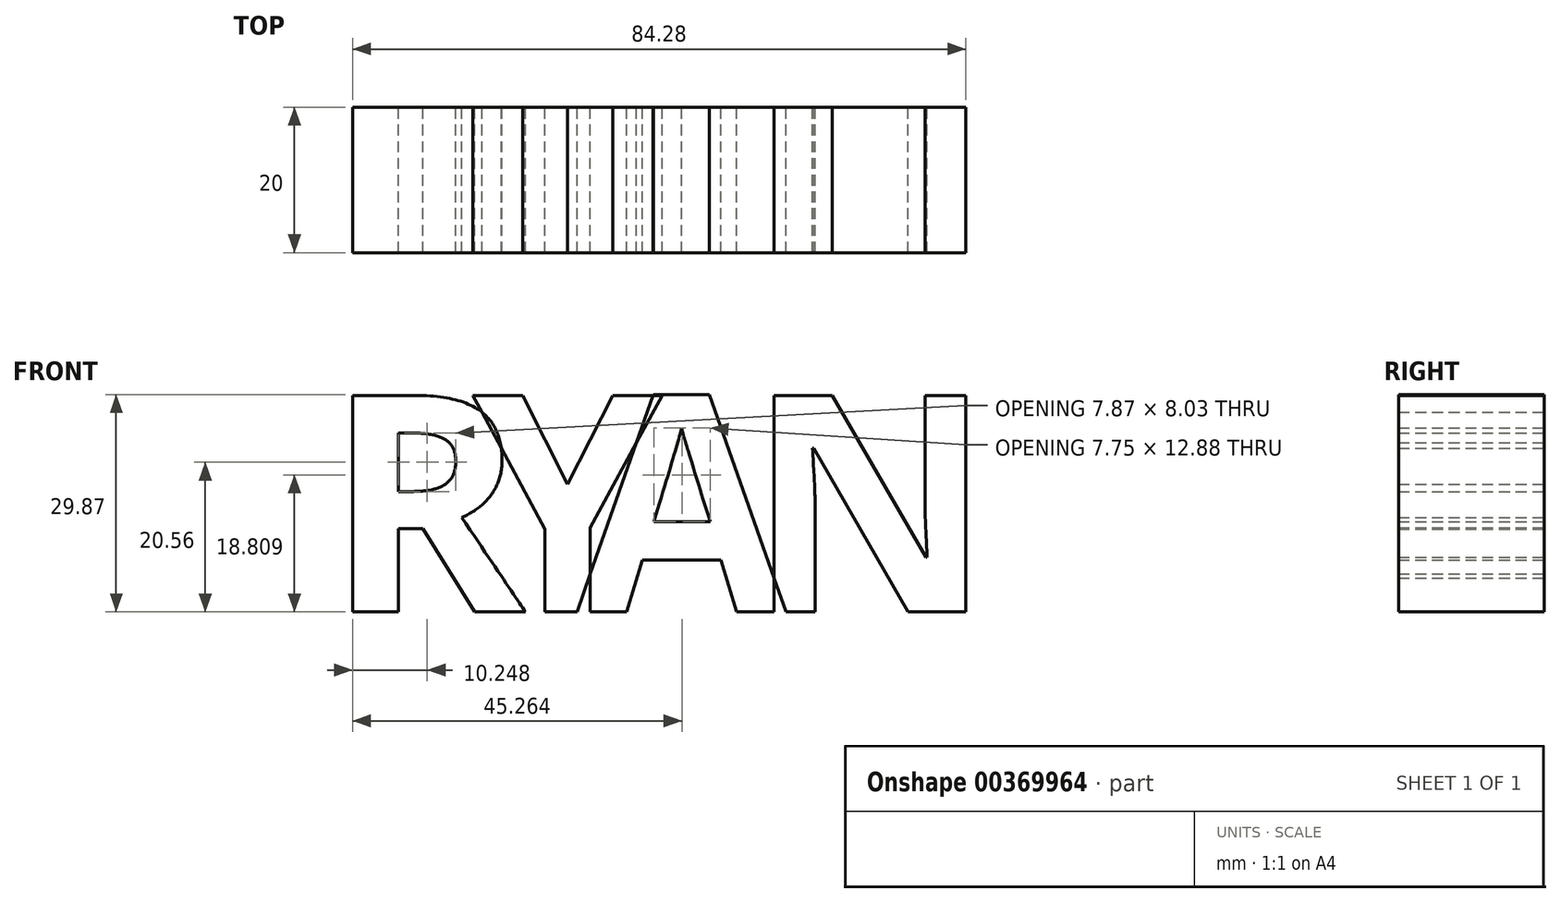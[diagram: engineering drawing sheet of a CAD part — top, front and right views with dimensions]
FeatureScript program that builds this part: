
annotation { "Feature Type Name" : "Feature", "Feature Type Description" : "" }
export const myFeature = defineFeature(function(context is Context, id is Id, definition is map)
    precondition{}
    {
        {
            var Q0;
            Q0=qCreatedBy(makeId("Front.planeOp"),FACE);
            var sketch = newSketch(context, id + "F0", { "sketchPlane" : qUnion([Q0])});
            skText(sketch, "E0", { "text": "R", "fontName": "OpenSans-Bold.ttf"});
            skText(sketch, "E1", { "text": "Y", "fontName": "OpenSans-Bold.ttf"});
            skText(sketch, "E2", { "text": "A", "fontName": "OpenSans-Bold.ttf"});
            skText(sketch, "E3", { "text": "N", "fontName": "OpenSans-Bold.ttf"});
            skLineSegment(sketch, "E4", {"start": v(-45.85, 30) * mm, "end": v(44.93, 30) * mm});
            skLineSegment(sketch, "E5.bottom", {"start": v(-42.18, 30) * mm, "end": v(42.17, 30) * mm});
            skLineSegment(sketch, "E5.top", {"start": v(-42.18, 0) * mm, "end": v(42.17, 0) * mm});
            skLineSegment(sketch, "E5.left", {"start": v(-42.18, 30) * mm, "end": v(-42.18, 0) * mm});
            skLineSegment(sketch, "E5.right", {"start": v(42.17, 30) * mm, "end": v(42.17, 0) * mm});
            skLineSegment(sketch, "E6", {"start": v(0, 0.2) * mm, "end": v(0, 0) * mm});
            const initialGuessF0  = {"E0": [-0.04585, 0, 1, 0, 0.03], "E1": [-0.02556, 0, 1, 0, 0.03], "E2": [-0.01126, 0, 1, 0, 0.03], "E3": [0.0121, 0, 1, 0, 0.03]};
            skSetInitialGuess(sketch, initialGuessF0);
            skSolve(sketch);
        }
        {
            var Q0;
            {var subQ11=sQuery(id+"F0.wireOp",EDGE,"E1.sketch_text.stroke-0");Q0=makeQuery(id+"F0.imprint","IMPRINT",FACE,{"disambiguationData":[TD([[makeQuery(id+"F0.imprint","IMPRINT",EDGE,{"derivedFrom":subQ11}),-1.0]])]});}
            var Q1;
            Q1=makeQuery(id+"F0.imprint","IMPRINT",FACE,{"disambiguationData":[TD([[makeQuery(id+"F0.imprint","IMPRINT",EDGE,{"derivedFrom":sQuery(id+"F0.wireOp",EDGE,"E0.sketch_text.stroke-0")}),-1.0]])]});
            var Q2;
            {var subQ11=sQuery(id+"F0.wireOp",EDGE,"E2.sketch_text.stroke-0");Q2=makeQuery(id+"F0.imprint","IMPRINT",FACE,{"disambiguationData":[TD([[makeQuery(id+"F0.imprint","IMPRINT",EDGE,{"derivedFrom":subQ11}),-1.0]])]});}
            var Q3;
            {var subQ6=sQuery(id+"F0.wireOp",EDGE,"E3.sketch_text.stroke-1");Q3=makeQuery(id+"F0.imprint","IMPRINT",FACE,{"disambiguationData":[TD([[makeQuery(id+"F0.imprint","IMPRINT",EDGE,{"derivedFrom":subQ6}),-1.0]])]});}
            extrude(context, id + "F1", {"entities" : qUnion([Q0, Q1, Q2, Q3]), "depth" : 20 * mm});
        }
        {
            var Q0;
            Q0=makeQuery(id+"F1.opExtrude","SWEPT_BODY",BODY,{"disambiguationData":[OSD([sQuery(id+"F0.wireOp",EDGE,"E0.sketch_text.stroke-0"),sQuery(id+"F0.wireOp",EDGE,"E0.sketch_text.stroke-1"),sQuery(id+"F0.wireOp",EDGE,"E0.sketch_text.stroke-2"),sQuery(id+"F0.wireOp",EDGE,"E0.sketch_text.stroke-3"),sQuery(id+"F0.wireOp",EDGE,"E0.sketch_text.stroke-4"),sQuery(id+"F0.wireOp",EDGE,"E0.sketch_text.stroke-5"),sQuery(id+"F0.wireOp",EDGE,"E0.sketch_text.stroke-6"),sQuery(id+"F0.wireOp",EDGE,"E0.sketch_text.stroke-7"),sQuery(id+"F0.wireOp",EDGE,"E0.sketch_text.stroke-8"),sQuery(id+"F0.wireOp",EDGE,"E0.sketch_text.stroke-9"),sQuery(id+"F0.wireOp",EDGE,"E0.sketch_text.stroke-10"),sQuery(id+"F0.wireOp",EDGE,"E0.sketch_text.stroke-11"),sQuery(id+"F0.wireOp",EDGE,"E0.sketch_text.stroke-12"),sQuery(id+"F0.wireOp",EDGE,"E0.sketch_text.stroke-13"),sQuery(id+"F0.wireOp",EDGE,"E0.sketch_text.stroke-14"),sQuery(id+"F0.wireOp",EDGE,"E0.sketch_text.stroke-15"),sQuery(id+"F0.wireOp",EDGE,"E0.sketch_text.stroke-16"),sQuery(id+"F0.wireOp",EDGE,"E0.sketch_text.stroke-17"),sQuery(id+"F0.wireOp",EDGE,"E0.sketch_text.stroke-18"),sQuery(id+"F0.wireOp",EDGE,"E1.sketch_text.stroke-0"),sQuery(id+"F0.wireOp",EDGE,"E1.sketch_text.stroke-1"),sQuery(id+"F0.wireOp",EDGE,"E1.sketch_text.stroke-2"),sQuery(id+"F0.wireOp",EDGE,"E1.sketch_text.stroke-3"),sQuery(id+"F0.wireOp",EDGE,"E1.sketch_text.stroke-4"),sQuery(id+"F0.wireOp",EDGE,"E1.sketch_text.stroke-5"),sQuery(id+"F0.wireOp",EDGE,"E1.sketch_text.stroke-6"),sQuery(id+"F0.wireOp",EDGE,"E1.sketch_text.stroke-7"),sQuery(id+"F0.wireOp",EDGE,"E1.sketch_text.stroke-8"),sQuery(id+"F0.wireOp",EDGE,"E2.sketch_text.stroke-0"),sQuery(id+"F0.wireOp",EDGE,"E2.sketch_text.stroke-1"),sQuery(id+"F0.wireOp",EDGE,"E2.sketch_text.stroke-2"),sQuery(id+"F0.wireOp",EDGE,"E2.sketch_text.stroke-3"),sQuery(id+"F0.wireOp",EDGE,"E2.sketch_text.stroke-4"),sQuery(id+"F0.wireOp",EDGE,"E2.sketch_text.stroke-5"),sQuery(id+"F0.wireOp",EDGE,"E2.sketch_text.stroke-6"),sQuery(id+"F0.wireOp",EDGE,"E2.sketch_text.stroke-7"),sQuery(id+"F0.wireOp",EDGE,"E2.sketch_text.stroke-8"),sQuery(id+"F0.wireOp",EDGE,"E2.sketch_text.stroke-9"),sQuery(id+"F0.wireOp",EDGE,"E2.sketch_text.stroke-10"),sQuery(id+"F0.wireOp",EDGE,"E2.sketch_text.stroke-11"),sQuery(id+"F0.wireOp",EDGE,"E3.sketch_text.stroke-0"),sQuery(id+"F0.wireOp",EDGE,"E3.sketch_text.stroke-1"),sQuery(id+"F0.wireOp",EDGE,"E3.sketch_text.stroke-2"),sQuery(id+"F0.wireOp",EDGE,"E3.sketch_text.stroke-3"),sQuery(id+"F0.wireOp",EDGE,"E3.sketch_text.stroke-4"),sQuery(id+"F0.wireOp",EDGE,"E3.sketch_text.stroke-5"),sQuery(id+"F0.wireOp",EDGE,"E3.sketch_text.stroke-6"),sQuery(id+"F0.wireOp",EDGE,"E3.sketch_text.stroke-7"),sQuery(id+"F0.wireOp",EDGE,"E3.sketch_text.stroke-8"),sQuery(id+"F0.wireOp",EDGE,"E3.sketch_text.stroke-9"),sQuery(id+"F0.wireOp",EDGE,"E3.sketch_text.stroke-10"),sQuery(id+"F0.wireOp",EDGE,"E3.sketch_text.stroke-11"),sQuery(id+"F0.wireOp",EDGE,"E3.sketch_text.stroke-12"),sQuery(id+"F0.wireOp",EDGE,"E3.sketch_text.stroke-13")])]});
            var Q1;
            Q1=makeQuery(id+"F1.opExtrude","SWEPT_BODY",BODY,{"disambiguationData":[OSD([sQuery(id+"F0.wireOp",EDGE,"E0.sketch_text.stroke-12"),sQuery(id+"F0.wireOp",EDGE,"E1.sketch_text.stroke-0"),sQuery(id+"F0.wireOp",EDGE,"E1.sketch_text.stroke-1"),sQuery(id+"F0.wireOp",EDGE,"E1.sketch_text.stroke-2"),sQuery(id+"F0.wireOp",EDGE,"E1.sketch_text.stroke-3"),sQuery(id+"F0.wireOp",EDGE,"E1.sketch_text.stroke-5"),sQuery(id+"F0.wireOp",EDGE,"E1.sketch_text.stroke-6"),sQuery(id+"F0.wireOp",EDGE,"E1.sketch_text.stroke-7"),sQuery(id+"F0.wireOp",EDGE,"E1.sketch_text.stroke-8"),sQuery(id+"F0.wireOp",EDGE,"E2.sketch_text.stroke-4"),sQuery(id+"F0.wireOp",EDGE,"E5.top")])]});
            var Q2;
            Q2=makeQuery(id+"F1.opExtrude","SWEPT_BODY",BODY,{"disambiguationData":[OSD([sQuery(id+"F0.wireOp",EDGE,"E1.sketch_text.stroke-1"),sQuery(id+"F0.wireOp",EDGE,"E1.sketch_text.stroke-2"),sQuery(id+"F0.wireOp",EDGE,"E1.sketch_text.stroke-3"),sQuery(id+"F0.wireOp",EDGE,"E2.sketch_text.stroke-0"),sQuery(id+"F0.wireOp",EDGE,"E2.sketch_text.stroke-1"),sQuery(id+"F0.wireOp",EDGE,"E2.sketch_text.stroke-2"),sQuery(id+"F0.wireOp",EDGE,"E2.sketch_text.stroke-4"),sQuery(id+"F0.wireOp",EDGE,"E2.sketch_text.stroke-5"),sQuery(id+"F0.wireOp",EDGE,"E2.sketch_text.stroke-6"),sQuery(id+"F0.wireOp",EDGE,"E2.sketch_text.stroke-8"),sQuery(id+"F0.wireOp",EDGE,"E2.sketch_text.stroke-9"),sQuery(id+"F0.wireOp",EDGE,"E2.sketch_text.stroke-10"),sQuery(id+"F0.wireOp",EDGE,"E2.sketch_text.stroke-11"),sQuery(id+"F0.wireOp",EDGE,"E3.sketch_text.stroke-6"),sQuery(id+"F0.wireOp",EDGE,"E5.top")])]});
            var Q3;
            Q3=makeQuery(id+"F1.opExtrude","SWEPT_BODY",BODY,{"disambiguationData":[OSD([sQuery(id+"F0.wireOp",EDGE,"E2.sketch_text.stroke-6"),sQuery(id+"F0.wireOp",EDGE,"E3.sketch_text.stroke-1"),sQuery(id+"F0.wireOp",EDGE,"E3.sketch_text.stroke-2"),sQuery(id+"F0.wireOp",EDGE,"E3.sketch_text.stroke-3"),sQuery(id+"F0.wireOp",EDGE,"E3.sketch_text.stroke-4"),sQuery(id+"F0.wireOp",EDGE,"E3.sketch_text.stroke-6"),sQuery(id+"F0.wireOp",EDGE,"E3.sketch_text.stroke-7"),sQuery(id+"F0.wireOp",EDGE,"E3.sketch_text.stroke-8"),sQuery(id+"F0.wireOp",EDGE,"E3.sketch_text.stroke-9"),sQuery(id+"F0.wireOp",EDGE,"E3.sketch_text.stroke-10"),sQuery(id+"F0.wireOp",EDGE,"E3.sketch_text.stroke-11"),sQuery(id+"F0.wireOp",EDGE,"E3.sketch_text.stroke-12"),sQuery(id+"F0.wireOp",EDGE,"E5.top"),sQuery(id+"F0.wireOp",EDGE,"E5.right")])]});
            transform(context, id + "F2", {"entities" : qUnion([Q0, Q1, Q2, Q3]), "transformType" : TransformType.TRANSLATION_3D, "dx" : 0 * mm, "dy" : 10 * mm, "dz" : 0 * mm, "makeCopy" : false});
        }
    });
